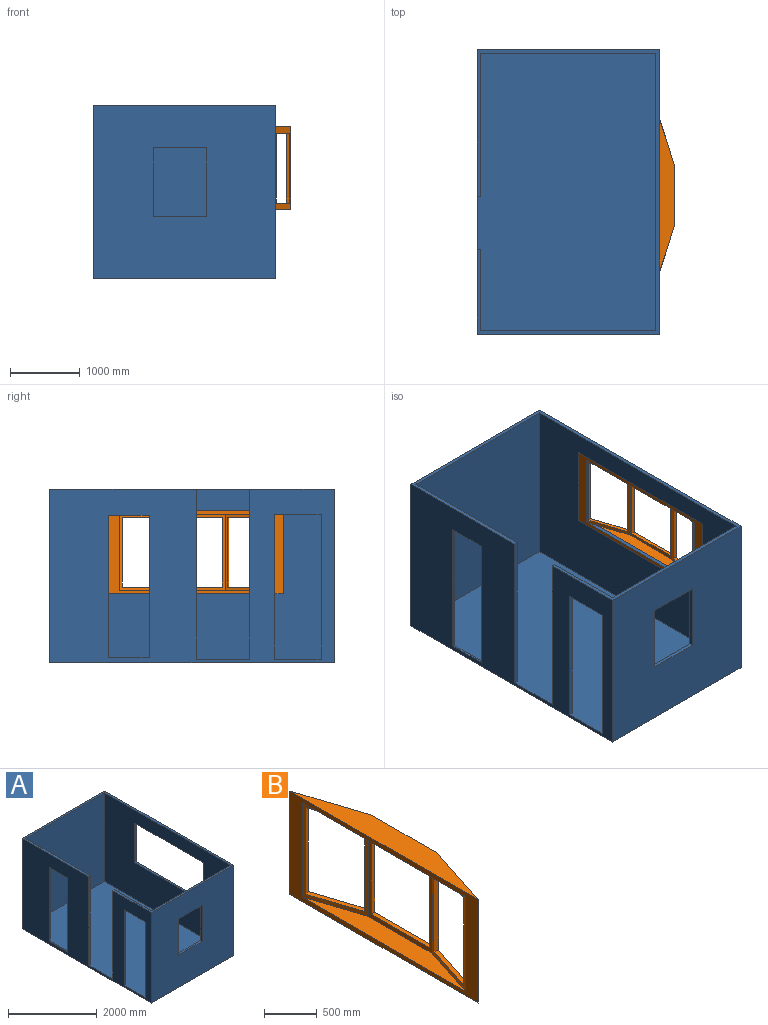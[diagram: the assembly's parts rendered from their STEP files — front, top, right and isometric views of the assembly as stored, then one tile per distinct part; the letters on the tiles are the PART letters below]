
ASSEMBLY  parts=2 mates=1
PART A: 33 faces, bbox 2616.2x4089.4x2489.2 mm
  f0: plane 2438.4x1168.4mm, normal (1,0,0), area 1447093.9mm2, adj f1,f5,f11,f24,f25,f26,f32
  f1: plane 4089.4x2616.2mm, normal (0,0,1), area 632256.8mm2, adj f0,f2,f3,f4,f5,f6,f7,f8
  f2: plane 4089.4x2489.2mm, normal (-1,0,0), area 5724827.3mm2, adj f1,f4,f8,f9,f11,f20,f21,f22
  f3: plane 2438.4x2057.4mm, normal (1,0,0), area 3720637.7mm2, adj f1,f10,f11,f27,f28,f29,f31
  f4: plane 2616.2x2489.2mm, normal (0,-1,0), area 5757407.8mm2, adj f1,f2,f6,f9,f16,f17,f18,f19
  f5: plane 2514.6x2438.4mm, normal (0,1,0), area 5376763.4mm2, adj f0,f1,f7,f11,f16,f17,f18,f19
  f6: plane 4089.4x2489.2mm, normal (1,0,0), area 7793532.8mm2, adj f1,f4,f8,f9,f12,f13,f14,f15
  f7: plane 3987.8x2438.4mm, normal (-1,0,0), area 7338049.8mm2, adj f1,f5,f10,f11,f12,f13,f14,f15
  f8: plane 2616.2x2489.2mm, normal (0,1,0), area 6512245mm2, adj f1,f2,f6,f9
  f9: plane 4089.4x2616.2mm, normal (0,0,-1), area 10698688.3mm2, adj f2,f4,f6,f8
  f10: plane 2514.6x2438.4mm, normal (0,-1,0), area 6131600.6mm2, adj f1,f3,f7,f11
  f11: plane 3987.8x2565.4mm, normal (0,0,1), area 10116431.4mm2, adj f0,f2,f3,f5,f7,f10,f24,f25
  f12: plane 1092.2x50.8mm, normal (0,1,0), area 55483.8mm2, adj f6,f7,f13,f15
  f13: plane 2184.4x50.8mm, normal (0,0,-1), area 110967.5mm2, adj f6,f7,f12,f14
  f14: plane 1092.2x50.8mm, normal (0,-1,0), area 55483.8mm2, adj f6,f7,f13,f15
  f15: plane 2184.4x50.8mm, normal (0,0,1), area 110967.5mm2, adj f6,f7,f12,f14
  f16: plane 990.6x50.8mm, normal (1,0,0), area 50322.5mm2, adj f4,f5,f17,f19
  f17: plane 762x50.8mm, normal (0,0,-1), area 38709.6mm2, adj f4,f5,f16,f18
  f18: plane 990.6x50.8mm, normal (-1,0,0), area 50322.5mm2, adj f4,f5,f17,f19
  f19: plane 762x50.8mm, normal (0,0,1), area 38709.6mm2, adj f4,f5,f16,f18
  f20: plane 2044.7x25.4mm, normal (0,1,0), area 51935.4mm2, adj f2,f21,f23,f30
  f21: plane 584.2x25.4mm, normal (0,0,1), area 14838.7mm2, adj f2,f20,f22,f30
  f22: plane 2044.7x25.4mm, normal (0,-1,0), area 51935.4mm2, adj f2,f21,f23,f30
  f23: plane 584.2x25.4mm, normal (0,0,-1), area 14838.7mm2, adj f2,f20,f22,f30
  f24: plane 2082.8x50.8mm, normal (0,-1,0), area 105806.2mm2, adj f0,f2,f11,f26
  f25: plane 2082.8x50.8mm, normal (0,1,0), area 105806.2mm2, adj f0,f2,f11,f26
  f26: plane 673.1x50.8mm, normal (0,0,-1), area 34193.5mm2, adj f0,f2,f24,f25
  f27: plane 622.3x25.4mm, normal (0,0,-1), area 15806.4mm2, adj f3,f28,f29,f30
  f28: plane 2082.8x25.4mm, normal (0,1,0), area 52903.1mm2, adj f3,f11,f27,f30
  f29: plane 2082.8x25.4mm, normal (0,-1,0), area 52903.1mm2, adj f3,f11,f27,f30
  f30: plane 2082.8x622.3mm, normal (1,0,0), area 101612.7mm2, adj f11,f20,f21,f22,f23,f27,f28,f29
  f31: plane 2438.4x50.8mm, normal (0,-1,0), area 123870.7mm2, adj f1,f2,f3,f11
  f32: plane 2438.4x50.8mm, normal (0,1,0), area 123870.7mm2, adj f0,f1,f2,f11
PART B: 23 faces, bbox 266.7x2514.2x1193.8 mm
  f0: plane 1193.8x823.63mm, normal (0.95,-0.31,0), area 406820.5mm2, adj f2,f3,f4,f5,f15,f16,f17,f18
  f1: plane 1092.2x666.75mm, normal (-0.95,0.31,0), area 138755.6mm2, adj f3,f7,f8,f9,f15,f16,f17,f18
  f2: plane 1193.8x866.94mm, normal (1,0,0), area 257695.9mm2, adj f0,f4,f5,f6,f11,f12,f13,f14
  f3: plane 2514.2x1193.8mm, normal (-1,0,0), area 615655.4mm2, adj f0,f1,f4,f5,f6,f7,f9,f10
  f4: plane 2514.2x266.7mm, normal (0,0,1), area 450875.5mm2, adj f0,f2,f3,f6
  f5: plane 2514.2x266.7mm, normal (0,0,-1), area 450875.5mm2, adj f0,f2,f3,f6
  f6: plane 1193.8x823.63mm, normal (0.95,0.31,0), area 406820.5mm2, adj f2,f3,f4,f5,f19,f20,f21,f22
  f7: plane 2184.4x215.9mm, normal (0,0,-1), area 327660.6mm2, adj f1,f3,f8,f10
  f8: plane 1092.2x850.9mm, normal (-1,0,0), area 152096.5mm2, adj f1,f7,f9,f10,f11,f12,f13,f14
  f9: plane 2184.4x215.9mm, normal (0,0,1), area 327660.6mm2, adj f1,f3,f8,f10
  f10: plane 1092.2x666.75mm, normal (-0.95,-0.31,0), area 138755.6mm2, adj f3,f7,f8,f9,f19,f20,f21,f22
  f11: plane 774.7x50.8mm, normal (0,0,1), area 39354.8mm2, adj f2,f8,f12,f14
  f12: plane 1003.3x50.8mm, normal (0,1,0), area 50967.6mm2, adj f2,f8,f11,f13
  f13: plane 774.7x50.8mm, normal (0,0,-1), area 39354.8mm2, adj f2,f8,f12,f14
  f14: plane 1003.3x50.8mm, normal (0,-1,0), area 50967.6mm2, adj f2,f8,f11,f13
  f15: plane 609.91x240.76mm, normal (0,0,-1), area 31731.4mm2, adj f0,f1,f16,f18
  f16: plane 1003.3x48.33mm, normal (-0.31,-0.95,0), area 50967.6mm2, adj f0,f1,f15,f17
  f17: plane 609.91x240.76mm, normal (0,0,1), area 31731.4mm2, adj f0,f1,f16,f18
  f18: plane 1003.3x48.33mm, normal (0.31,0.95,0), area 50967.6mm2, adj f0,f1,f15,f17
  f19: plane 1003.3x48.33mm, normal (0.31,-0.95,0), area 50967.6mm2, adj f6,f10,f20,f22
  f20: plane 609.91x240.76mm, normal (0,0,1), area 31731.4mm2, adj f6,f10,f19,f21
  f21: plane 1003.3x48.33mm, normal (-0.31,0.95,0), area 50967.6mm2, adj f6,f10,f20,f22
  f22: plane 609.91x240.76mm, normal (0,0,-1), area 31731.4mm2, adj f6,f10,f19,f21
PLACE A at identity
PLACE B t=(1414.74,-1015.76,990.6)mm
MATE fastened B.f3 <-> A.f7  axis (-1,0,0) through (1414.74,76.44,2082.8)mm
